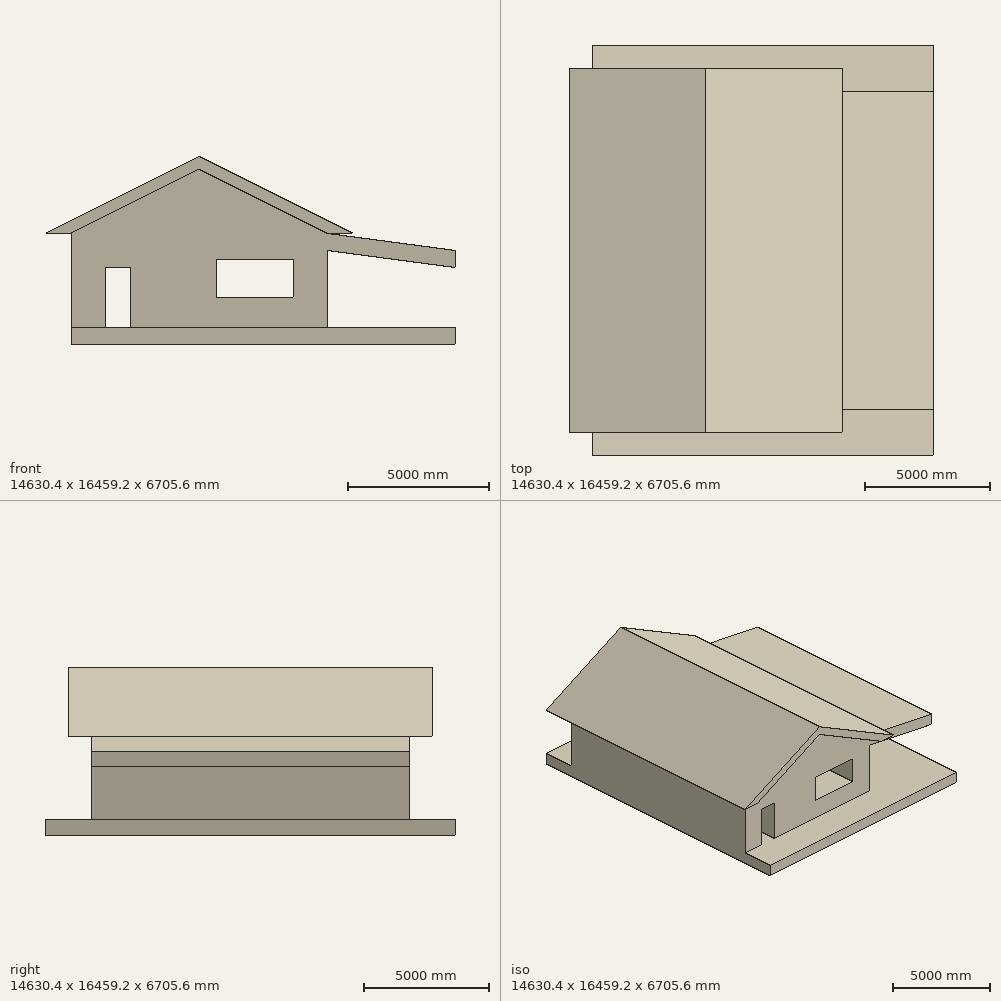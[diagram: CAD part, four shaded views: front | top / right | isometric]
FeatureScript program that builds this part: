
annotation { "Feature Type Name" : "Feature", "Feature Type Description" : "" }
export const myFeature = defineFeature(function(context is Context, id is Id, definition is map)
    precondition{}
    {
        {
            var Q0;
            Q0=qCreatedBy(makeId("Front.planeOp"),FACE);
            var sketch = newSketch(context, id + "F0", { "sketchPlane" : qUnion([Q0])});
            skLineSegment(sketch, "E0", {"start": v(0, 0) * mm, "end": v(4572, 0) * mm});
            skLineSegment(sketch, "E1", {"start": v(4572, 0) * mm, "end": v(4572, 2286) * mm});
            skLineSegment(sketch, "E2", {"start": v(4572, 0) * mm, "end": v(9144, 0) * mm});
            skLineSegment(sketch, "E3", {"start": v(0, 0) * mm, "end": v(4572, 2286) * mm});
            skLineSegment(sketch, "E4", {"start": v(4572, 2286) * mm, "end": v(9144, 0) * mm});
            skLineSegment(sketch, "E5", {"start": v(9144, 0) * mm, "end": v(10058.4, 0) * mm});
            skLineSegment(sketch, "E6", {"start": v(0, 0) * mm, "end": v(-914.4, 0) * mm});
            skLineSegment(sketch, "E7", {"start": v(4572, 2286) * mm, "end": v(4572, 2743.2) * mm});
            skLineSegment(sketch, "E8", {"start": v(-914.4, 0) * mm, "end": v(4572, 2743.2) * mm});
            skLineSegment(sketch, "E9", {"start": v(4572, 2743.2) * mm, "end": v(10058.4, 0) * mm});
            skLineSegment(sketch, "E10", {"start": v(0, 0) * mm, "end": v(0, -3352.8) * mm});
            skLineSegment(sketch, "E11", {"start": v(9144, 0) * mm, "end": v(9144, -3352.8) * mm});
            skLineSegment(sketch, "E12", {"start": v(0, -3352.8) * mm, "end": v(9144, -3352.8) * mm});
            skLineSegment(sketch, "E13", {"start": v(0, -3352.8) * mm, "end": v(0, -3962.4) * mm});
            skLineSegment(sketch, "E14", {"start": v(9144, -3352.8) * mm, "end": v(9144, -3962.4) * mm});
            skLineSegment(sketch, "E15", {"start": v(0, -3962.4) * mm, "end": v(9144, -3962.4) * mm});
            skLineSegment(sketch, "E16", {"start": v(9144, -3962.4) * mm, "end": v(13716, -3962.4) * mm});
            skLineSegment(sketch, "E17", {"start": v(13716, -3962.4) * mm, "end": v(13716, -3352.8) * mm});
            skLineSegment(sketch, "E18", {"start": v(9144, -3352.8) * mm, "end": v(13716, -3352.8) * mm});
            skLineSegment(sketch, "E19", {"start": v(13716, -3352.8) * mm, "end": v(13716, -609.6) * mm});
            skLineSegment(sketch, "E20", {"start": v(9144, 0) * mm, "end": v(13716, -609.6) * mm});
            skLineSegment(sketch, "E21", {"start": v(9144, 0) * mm, "end": v(9144, -609.6) * mm});
            skLineSegment(sketch, "E22", {"start": v(13716, -609.6) * mm, "end": v(13716, -1219.2) * mm});
            skLineSegment(sketch, "E23", {"start": v(9144, -609.6) * mm, "end": v(13716, -1219.2) * mm});
            skLineSegment(sketch, "E24.bottom", {"start": v(5181.6, -914.4) * mm, "end": v(7924.8, -914.4) * mm});
            skLineSegment(sketch, "E24.left", {"start": v(5181.6, -914.4) * mm, "end": v(5181.6, -2286) * mm});
            skLineSegment(sketch, "E24.right", {"start": v(7924.8, -914.4) * mm, "end": v(7924.8, -2286) * mm});
            skLineSegment(sketch, "E25", {"start": v(5181.6, -2286) * mm, "end": v(7924.8, -2286) * mm});
            skLineSegment(sketch, "E26.bottom", {"start": v(10668, -1219.2) * mm, "end": v(11887.2, -1219.2) * mm});
            skLineSegment(sketch, "E26.top", {"start": v(10668, -2590.8) * mm, "end": v(11887.2, -2590.8) * mm});
            skLineSegment(sketch, "E26.left", {"start": v(10668, -1219.2) * mm, "end": v(10668, -2590.8) * mm});
            skLineSegment(sketch, "E26.right", {"start": v(11887.2, -1219.2) * mm, "end": v(11887.2, -2590.8) * mm});
            skLineSegment(sketch, "E27.bottom", {"start": v(1219.2, -1219.2) * mm, "end": v(2133.6, -1219.2) * mm});
            skLineSegment(sketch, "E27.top", {"start": v(1219.2, -3352.8) * mm, "end": v(2133.6, -3352.8) * mm});
            skLineSegment(sketch, "E27.left", {"start": v(1219.2, -1219.2) * mm, "end": v(1219.2, -3352.8) * mm});
            skLineSegment(sketch, "E27.right", {"start": v(2133.6, -1219.2) * mm, "end": v(2133.6, -3352.8) * mm});
            skSolve(sketch);
        }
        {
            var Q0;
            Q0=makeQuery(id+"F0.imprint","IMPRINT",FACE,{"disambiguationData":[TD([[makeQuery(id+"F0.imprint","IMPRINT",EDGE,{"derivedFrom":sQuery(id+"F0.wireOp",EDGE,"E3")}),1.0]])]});
            var Q1;
            Q1=makeQuery(id+"F0.imprint","IMPRINT",FACE,{"disambiguationData":[TD([[makeQuery(id+"F0.imprint","IMPRINT",EDGE,{"derivedFrom":sQuery(id+"F0.wireOp",EDGE,"E4")}),1.0]])]});
            extrude(context, id + "F1", {"entities" : qUnion([Q0, Q1]), "endBound" : BoundingType.SYMMETRIC, "depth" : 14630.4 * mm, "offsetDistance" : 30.48 * mm});
        }
        {
            var Q0;
            Q0=makeQuery(id+"F0.imprint","IMPRINT",FACE,{"disambiguationData":[TD([[makeQuery(id+"F0.imprint","IMPRINT",EDGE,{"derivedFrom":sQuery(id+"F0.wireOp",EDGE,"E0")}),1.0]])]});
            var Q1;
            Q1=makeQuery(id+"F0.imprint","IMPRINT",FACE,{"disambiguationData":[TD([[makeQuery(id+"F0.imprint","IMPRINT",EDGE,{"derivedFrom":sQuery(id+"F0.wireOp",EDGE,"E1")}),-1.0]])]});
            extrude(context, id + "F2", {"entities" : qUnion([Q0, Q1]), "operationType" : NewBodyOperationType.ADD, "endBound" : BoundingType.SYMMETRIC, "depth" : 12801.6 * mm, "offsetDistance" : 30.48 * mm});
        }
        {
            var Q0;
            Q0=makeQuery(id+"F0.imprint","IMPRINT",FACE,{"disambiguationData":[TD([[makeQuery(id+"F0.imprint","IMPRINT",EDGE,{"derivedFrom":sQuery(id+"F0.wireOp",EDGE,"E0")}),-1.0]])]});
            extrude(context, id + "F3", {"entities" : qUnion([Q0]), "operationType" : NewBodyOperationType.ADD, "endBound" : BoundingType.SYMMETRIC, "depth" : 12801.6 * mm, "offsetDistance" : 30.48 * mm});
        }
        {
            var Q0;
            Q0=makeQuery(id+"F0.imprint","IMPRINT",FACE,{"disambiguationData":[TD([[makeQuery(id+"F0.imprint","IMPRINT",EDGE,{"derivedFrom":sQuery(id+"F0.wireOp",EDGE,"E20")}),-1.0]])]});
            extrude(context, id + "F4", {"entities" : qUnion([Q0]), "operationType" : NewBodyOperationType.ADD, "endBound" : BoundingType.SYMMETRIC, "depth" : 12801.6 * mm, "offsetDistance" : 30.48 * mm});
        }
        {
            var Q0;
            Q0=makeQuery(id+"F0.imprint","IMPRINT",FACE,{"disambiguationData":[TD([[makeQuery(id+"F0.imprint","IMPRINT",EDGE,{"derivedFrom":sQuery(id+"F0.wireOp",EDGE,"E11")}),1.0]])]});
            extrude(context, id + "F5", {"entities" : qUnion([Q0]), "operationType" : NewBodyOperationType.ADD, "endBound" : BoundingType.SYMMETRIC, "depth" : 12192 * mm, "offsetDistance" : 30.48 * mm});
        }
        {
            var Q0;
            Q0=makeQuery(id+"F0.imprint","IMPRINT",FACE,{"disambiguationData":[TD([[makeQuery(id+"F0.imprint","IMPRINT",EDGE,{"derivedFrom":sQuery(id+"F0.wireOp",EDGE,"E14")}),1.0]])]});
            var Q1;
            {var subQ1=sQuery(id+"F0.wireOp",EDGE,"E13");Q1=makeQuery(id+"F0.imprint","IMPRINT",FACE,{"disambiguationData":[TD([[makeQuery(id+"F0.imprint","IMPRINT",EDGE,{"derivedFrom":subQ1}),1.0]])]});}
            extrude(context, id + "F6", {"entities" : qUnion([Q0, Q1]), "operationType" : NewBodyOperationType.ADD, "endBound" : BoundingType.SYMMETRIC, "depth" : 16459.2 * mm, "offsetDistance" : 30.48 * mm});
        }
    });
